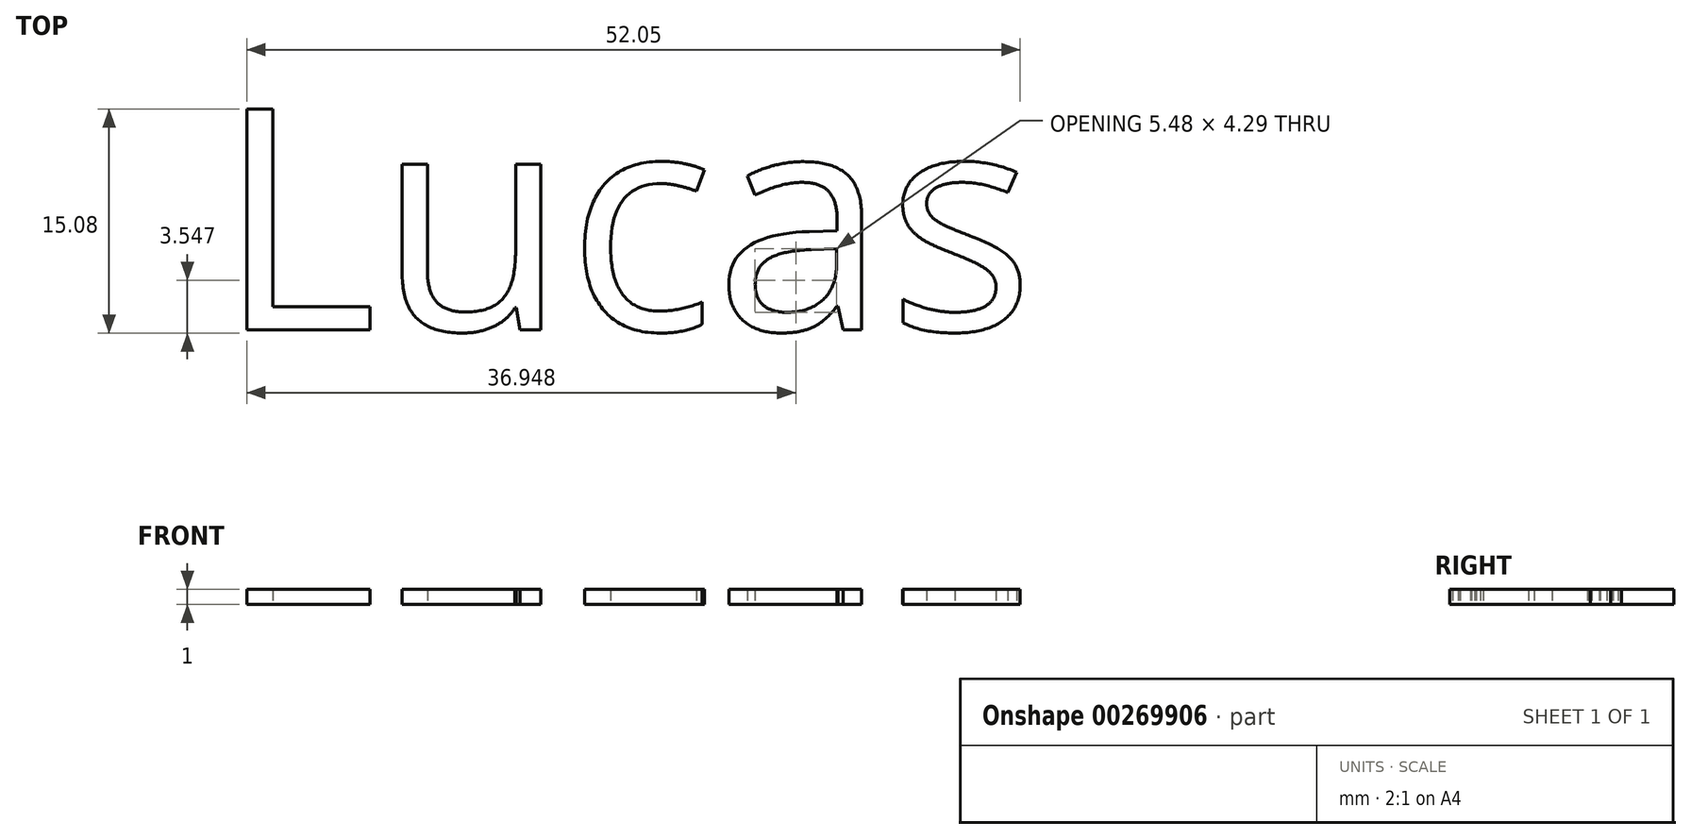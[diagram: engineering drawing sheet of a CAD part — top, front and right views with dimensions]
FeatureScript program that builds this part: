
annotation { "Feature Type Name" : "Feature", "Feature Type Description" : "" }
export const myFeature = defineFeature(function(context is Context, id is Id, definition is map)
    precondition{}
    {
        {
            var Q0;
            Q0=qCreatedBy(makeId("Top.planeOp"),FACE);
            var sketch = newSketch(context, id + "F0", { "sketchPlane" : qUnion([Q0])});
            skText(sketch, "E0", { "text": "Lucas", "fontName": "OpenSans-Regular.ttf"});
            const initialGuessF0  = {"E0": [-0.02374, 0.00129, 1, 0, 0.015]};
            skSetInitialGuess(sketch, initialGuessF0);
            skSolve(sketch);
        }
        {
            var Q0;
            Q0 = qSketchRegion(id + "F0", true);
            extrude(context, id + "F1", {"entities" : qUnion([Q0]), "depth" : 1 * mm});
        }
    });
